# Revit family: Emeco_Alfi_3-Seat Bench_ALFIH_By Jasper Morrison
name_source: partatom
category: Furniture
revit_build: Autodesk Revit Architecture 2012 (Build: 20120126_0600(x64)
units: mm (PartAtom-declared; Revit-internal decimal feet)

## types (5) — shared parameters
Assembly Code = E2020200
Collaborator = Jasper Morrison
Depth = 19 3/4"
Durability = Durability and strength test ANSI/BIFMA X5.1
Frame Finish = EMECO-Ash Wood
Frame Material = EMECO-Responsibly Harvested Ash Wood
Glides = EMECO-Lexan® Glides
Height = 31 1/4"
Made In = USA
Manufacturer = Emeco
Outdoor Warranty = 2 Years
Product Name = Alfi 3-Seat Bench, High Back
SKU = ALFIH
Seat Height = 18"
Seat Material = EMECO-100% reclaimed post-industrial waste –92.5% reclaimed polypropylene, 7.5% reclaimed wood fiber
URL = www.emeco.net
Warranties = 2 Year Warranty
Weight (lbs) = 40.2
Width = 66 1/2"

## per-type parameters (varying)
| type | Seat & Back Finish |
| ALFIH-DARK GREY | EMECO-Polypropylen-Dark Gray |
| ALFIH-SAND | EMECO-Polypropylen-Sand |
| ALFIH-GREEN | EMECO-Polypropylen-Green |
| ALFIH-DARK BROWN | EMECO-Polypropylen-Dark Brown |
| ALFIH-RED | EMECO-Polypropylen-Red |

note: column(s) folded — value = type name in every type: Model

## geometry (parser evidence)
native form markers: Blend x14, Sweep x2
no freeform markers — native parametric forms only
